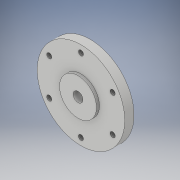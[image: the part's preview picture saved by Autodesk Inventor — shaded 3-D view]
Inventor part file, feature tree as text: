
AUTODESK INVENTOR PART (.ipt)
format: ipt  version: 2017 (Build 210142000, 142)  size: 150,528 bytes
history: native  units: in
note: dims shown in document units (in); Inventor stores cm internally (conversion verified against a paired STEP export)
features: sketch x7, extrude x3, hole x3, pattern_circular x1, plane x1
ambient origin geometry x8: Origin, YZ Plane, XZ Plane, XY Plane, X Axis, Y Axis, Z Axis, Center Point
bodies: Solid1 (feature_tree)
feature tree (15):
  extrude  "Extrusion1"  Depth=0.236in TaperAngle=0.0deg
  hole  "Hole1"  [1 undecoded]
  hole  "Hole2"  [1 undecoded]
  pattern_circular  "Circular Pattern1"  [2 undecoded]
  extrude  "Extrusion2"  [1 undecoded]
  extrude  "Extrusion3"  [1 undecoded]
  sketch  "Sketch6"  dims[d25=0.4134in]
  plane  "Work Plane1"
  hole  "Hole3"  [1 undecoded]
  sketch  "Sketch1"  dims[d0=2.236in d1=0.236in d2=0.0in]
  sketch  "Sketch2"  dims[d3=0.25in d4=0.75in d5=0.375in d6=0.25in d7=0.5635in d8=0.236in d9=0.0in d10=0.935in]
  sketch  "Sketch3"  dims[d12=0.13in d13=0.328in d14=0.375in d15=0.25in d16=0.5635in d17=0.484in d18=0.8108in d19=2.3622in d20=360.0deg]
  sketch  "Sketch4"  dims[d22=0.944in]
  sketch  "Sketch5"  dims[d23=0.075in d24=0.0in]
  sketch  "Sketch7"  dims[d26=0.3in d27=0.0in d28=0.15in d29=0.156in d30=0.25in d31=0.375in d32=0.25in d33=0.5635in d34=0.25in d35=0.8108in]
note: 7 required parameter values undecoded (feature->parameter linkage not recoverable at this tier; creation-order binding heuristic only, values carry confidence <= 0.55)
